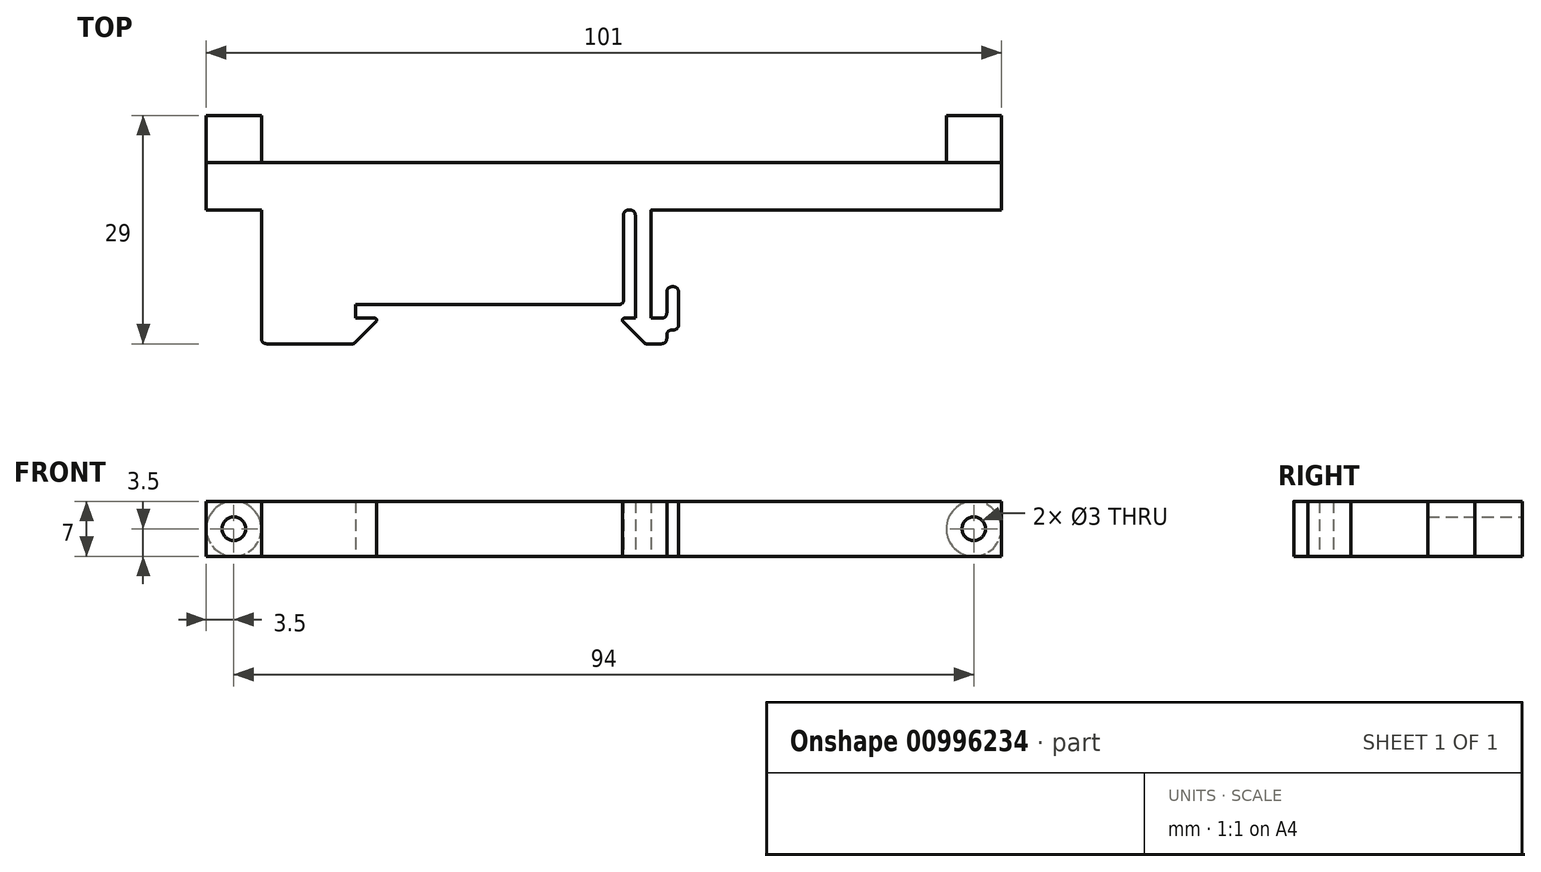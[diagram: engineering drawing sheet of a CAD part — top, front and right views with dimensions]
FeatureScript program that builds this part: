
annotation { "Feature Type Name" : "Feature", "Feature Type Description" : "" }
export const myFeature = defineFeature(function(context is Context, id is Id, definition is map)
    precondition{}
    {
        {
            var Q0;
            Q0=qCreatedBy(makeId("Top.planeOp"),FACE);
            var sketch = newSketch(context, id + "F0", { "sketchPlane" : qUnion([Q0])});
            skLineSegment(sketch, "E0", {"start": v(0, 0) * mm, "end": v(33.5, 0) * mm});
            skLineSegment(sketch, "E1", {"start": v(34, 0.5) * mm, "end": v(34, 11.35) * mm});
            skLineSegment(sketch, "E2", {"start": v(34.65, 12) * mm, "end": v(34.85, 12) * mm});
            skLineSegment(sketch, "E3", {"start": v(35.5, 11.35) * mm, "end": v(35.5, -1.75) * mm});
            skLineSegment(sketch, "E4", {"start": v(35.5, -1.75) * mm, "end": v(34.1, -1.75) * mm});
            skLineSegment(sketch, "E5", {"start": v(33.93, -2.18) * mm, "end": v(36.68, -4.93) * mm});
            skLineSegment(sketch, "E6", {"start": v(36.85, -5) * mm, "end": v(38.85, -5) * mm});
            skLineSegment(sketch, "E7", {"start": v(39.5, -4.35) * mm, "end": v(39.5, -3.9) * mm});
            skLineSegment(sketch, "E8", {"start": v(40.15, -3.25) * mm, "end": v(40.35, -3.25) * mm});
            skLineSegment(sketch, "E9", {"start": v(41, -2.6) * mm, "end": v(41, 1.6) * mm});
            skLineSegment(sketch, "E10", {"start": v(40.35, 2.25) * mm, "end": v(40.15, 2.25) * mm});
            skLineSegment(sketch, "E11", {"start": v(39.5, 1.6) * mm, "end": v(39.5, -1.1) * mm});
            skLineSegment(sketch, "E12", {"start": v(38.85, -1.75) * mm, "end": v(37.5, -1.75) * mm});
            skLineSegment(sketch, "E13", {"start": v(37.5, -1.75) * mm, "end": v(37.5, 11.96) * mm});
            skLineSegment(sketch, "E14", {"start": v(37.54, 12) * mm, "end": v(82, 12) * mm});
            skLineSegment(sketch, "E15", {"start": v(82, 12) * mm, "end": v(82, 18) * mm});
            skLineSegment(sketch, "E16", {"start": v(82, 18) * mm, "end": v(-19, 18) * mm});
            skLineSegment(sketch, "E17", {"start": v(-19, 18) * mm, "end": v(-19, 12) * mm});
            skLineSegment(sketch, "E18", {"start": v(-19, 12) * mm, "end": v(-12, 12) * mm});
            skLineSegment(sketch, "E19", {"start": v(-12, 12) * mm, "end": v(-12, -4.35) * mm});
            skLineSegment(sketch, "E20", {"start": v(-11.35, -5) * mm, "end": v(-0.35, -5) * mm});
            skLineSegment(sketch, "E21", {"start": v(-0.18, -4.93) * mm, "end": v(2.57, -2.18) * mm});
            skLineSegment(sketch, "E22", {"start": v(2.4, -1.75) * mm, "end": v(0, -1.75) * mm});
            skLineSegment(sketch, "E23", {"start": v(0, -1.75) * mm, "end": v(0, 0) * mm});
            skPoint(sketch, "E24.visualSharp", {"position": v(-0.25, -5) * mm});
            skArc(sketch, "E24.filletArc", {"start": v(-0.35, -5) * mm, "mid": v(-0.26, -4.98) * mm, "end": v(-0.18, -4.93) * mm});
            skPoint(sketch, "E25.visualSharp", {"position": v(3, -1.75) * mm});
            skArc(sketch, "E25.filletArc", {"start": v(2.57, -2.18) * mm, "mid": v(2.63, -1.9) * mm, "end": v(2.4, -1.75) * mm});
            skPoint(sketch, "E26.visualSharp", {"position": v(33.5, -1.75) * mm});
            skArc(sketch, "E26.filletArc", {"start": v(34.1, -1.75) * mm, "mid": v(33.87, -1.9) * mm, "end": v(33.93, -2.18) * mm});
            skPoint(sketch, "E27.visualSharp", {"position": v(36.75, -5) * mm});
            skArc(sketch, "E27.filletArc", {"start": v(36.68, -4.93) * mm, "mid": v(36.76, -4.98) * mm, "end": v(36.85, -5) * mm});
            skPoint(sketch, "E28.visualSharp", {"position": v(34, 12) * mm});
            skArc(sketch, "E28.filletArc", {"start": v(34.65, 12) * mm, "mid": v(34.2, 11.8) * mm, "end": v(34, 11.35) * mm});
            skPoint(sketch, "E29.visualSharp", {"position": v(35.5, 12) * mm});
            skArc(sketch, "E29.filletArc", {"start": v(35.5, 11.35) * mm, "mid": v(35.3, 11.8) * mm, "end": v(34.85, 12) * mm});
            skPoint(sketch, "E30.visualSharp", {"position": v(-12, -5) * mm});
            skArc(sketch, "E30.filletArc", {"start": v(-12, -4.35) * mm, "mid": v(-11.8, -4.8) * mm, "end": v(-11.35, -5) * mm});
            skPoint(sketch, "E31.visualSharp", {"position": v(39.5, -5) * mm});
            skArc(sketch, "E31.filletArc", {"start": v(38.85, -5) * mm, "mid": v(39.3, -4.8) * mm, "end": v(39.5, -4.35) * mm});
            skPoint(sketch, "E32.visualSharp", {"position": v(39.5, -3.25) * mm});
            skArc(sketch, "E32.filletArc", {"start": v(40.15, -3.25) * mm, "mid": v(39.7, -3.44) * mm, "end": v(39.5, -3.9) * mm});
            skPoint(sketch, "E33.visualSharp", {"position": v(41, -3.25) * mm});
            skArc(sketch, "E33.filletArc", {"start": v(40.35, -3.25) * mm, "mid": v(40.8, -3.06) * mm, "end": v(41, -2.6) * mm});
            skPoint(sketch, "E34.visualSharp", {"position": v(39.5, -1.75) * mm});
            skArc(sketch, "E34.filletArc", {"start": v(38.85, -1.75) * mm, "mid": v(39.3, -1.56) * mm, "end": v(39.5, -1.1) * mm});
            skPoint(sketch, "E35.visualSharp", {"position": v(41, 2.25) * mm});
            skArc(sketch, "E35.filletArc", {"start": v(41, 1.6) * mm, "mid": v(40.8, 2.06) * mm, "end": v(40.35, 2.25) * mm});
            skPoint(sketch, "E36.visualSharp", {"position": v(39.5, 2.25) * mm});
            skArc(sketch, "E36.filletArc", {"start": v(40.15, 2.25) * mm, "mid": v(39.7, 2.06) * mm, "end": v(39.5, 1.6) * mm});
            skPoint(sketch, "E37.visualSharp", {"position": v(34, 0) * mm});
            skArc(sketch, "E37.filletArc", {"start": v(33.5, 0) * mm, "mid": v(33.85, 0.15) * mm, "end": v(34, 0.5) * mm});
            skPoint(sketch, "E38.visualSharp", {"position": v(37.5, 12) * mm});
            skArc(sketch, "E38.filletArc", {"start": v(37.54, 12) * mm, "mid": v(37.51, 11.99) * mm, "end": v(37.5, 11.96) * mm});
            skSolve(sketch);
        }
        {
            var Q0;
            Q0 = qSketchRegion(id + "F0", true);
            extrude(context, id + "F1", {"entities" : qUnion([Q0]), "depth" : 7 * mm, "offsetDistance" : 25 * mm, "symmetric" : true});
        }
        {
            var Q0;
            Q0=makeQuery(id+"F1.opExtrude","SWEPT_FACE",FACE,{"disambiguationData":[OSD([sQuery(id+"F0.wireOp",EDGE,"E16")])]});
            var sketch = newSketch(context, id + "F2", { "sketchPlane" : qUnion([Q0])});
            skCircle(sketch, "E39", {"center": v(-78.5, 0) * mm, "radius": 3.5 * mm});
            skCircle(sketch, "E40", {"center": v(15.5, 0) * mm, "radius": 3.5 * mm});
            skSolve(sketch);
        }
        {
            var Q0;
            Q0 = qSketchRegion(id + "F2", true);
            extrude(context, id + "F3", {"entities" : qUnion([Q0]), "operationType" : NewBodyOperationType.ADD, "depth" : 6 * mm, "offsetDistance" : 25 * mm});
        }
        {
            var Q0;
            Q0=makeQuery(id+"F3.opExtrude","CAP_FACE",FACE,{"disambiguationData":[OSD([sQuery(id+"F2.wireOp",EDGE,"E39")])],"isStart":false});
            var sketch = newSketch(context, id + "F4", { "sketchPlane" : qUnion([Q0])});
            skCircle(sketch, "E41", {"center": v(-78.5, 0) * mm, "radius": 1.5 * mm});
            skCircle(sketch, "E42", {"center": v(15.5, 0) * mm, "radius": 1.5 * mm});
            skSolve(sketch);
        }
        {
            var Q0;
            Q0 = qSketchRegion(id + "F4", true);
            extrude(context, id + "F5", {"entities" : qUnion([Q0]), "operationType" : NewBodyOperationType.REMOVE, "endBound" : BoundingType.THROUGH_ALL, "oppositeDirection" : true, "depth" : 25 * mm, "offsetDistance" : 25 * mm});
        }
    });
